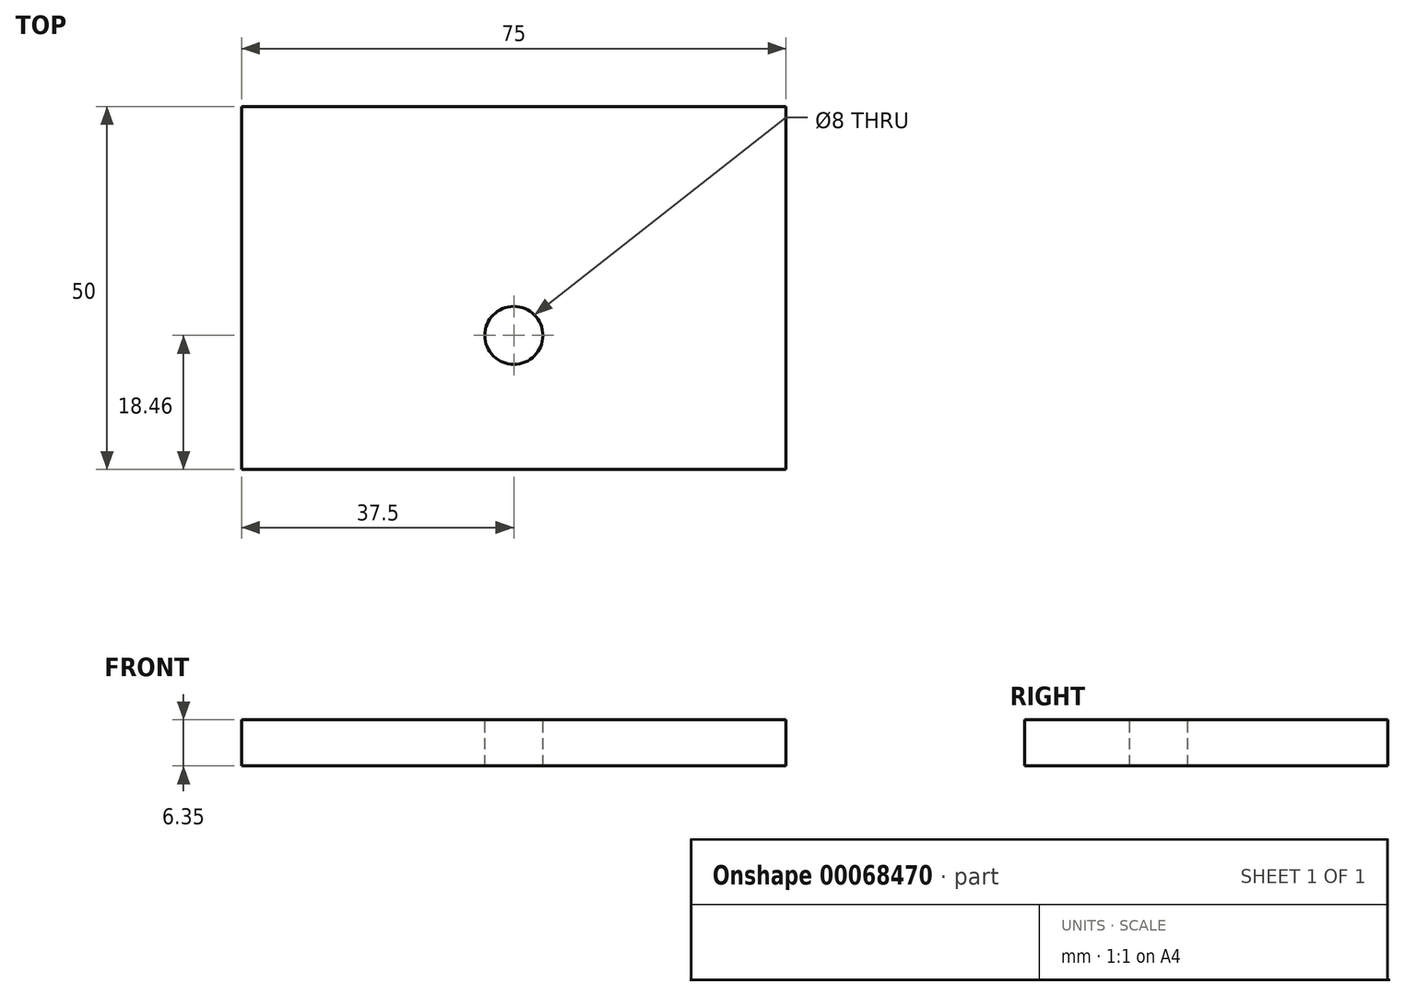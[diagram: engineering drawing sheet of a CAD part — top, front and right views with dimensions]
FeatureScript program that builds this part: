
annotation { "Feature Type Name" : "Feature", "Feature Type Description" : "" }
export const myFeature = defineFeature(function(context is Context, id is Id, definition is map)
    precondition{}
    {
        {
            var Q0;
            Q0=qCreatedBy(makeId("Top.planeOp"),FACE);
            var sketch = newSketch(context, id + "F0", { "sketchPlane" : qUnion([Q0])});
            skLineSegment(sketch, "E0.rect.bottom", {"start": v(37.5, 25) * mm, "end": v(-37.5, 25) * mm});
            skLineSegment(sketch, "E0.rect.top", {"start": v(37.5, -25) * mm, "end": v(-37.5, -25) * mm});
            skLineSegment(sketch, "E0.rect.left", {"start": v(37.5, 25) * mm, "end": v(37.5, -25) * mm});
            skLineSegment(sketch, "E0.rect.right", {"start": v(-37.5, 25) * mm, "end": v(-37.5, -25) * mm});
            skPoint(sketch, "E0.rect.middle", {"position": v(0, 0) * mm});
            skSolve(sketch);
        }
        {
            var Q0;
            Q0=makeQuery(id+"F0.imprint","IMPRINT",FACE,{"disambiguationData":[TD([[makeQuery(id+"F0.imprint","IMPRINT",EDGE,{"derivedFrom":sQuery(id+"F0.wireOp",EDGE,"E0.rect.bottom")}),1.0]])]});
            extrude(context, id + "F1", {"entities" : qUnion([Q0]), "depth" : 6.35 * mm});
        }
        {
            var Q0;
            Q0=makeQuery(id+"F1.opExtrude","CAP_FACE",FACE,{"disambiguationData":[OSD([sQuery(id+"F0.wireOp",EDGE,"E0.rect.bottom"),sQuery(id+"F0.wireOp",EDGE,"E0.rect.top"),sQuery(id+"F0.wireOp",EDGE,"E0.rect.left"),sQuery(id+"F0.wireOp",EDGE,"E0.rect.right")])],"isStart":false});
            var sketch = newSketch(context, id + "F2", { "sketchPlane" : qUnion([Q0])});
            skCircle(sketch, "E1", {"center": v(0, -6.54) * mm, "radius": 4 * mm});
            skPoint(sketch, "E2.end.orphan", {"position": v(0, -25) * mm});
            skPoint(sketch, "E2.start.orphan", {"position": v(0, -10.54) * mm});
            skLineSegment(sketch, "E3", {"start": v(0, -2.54) * mm, "end": v(0, 0) * mm});
            skLineSegment(sketch, "E4", {"start": v(0, -10.54) * mm, "end": v(0, -25) * mm});
            skSolve(sketch);
        }
        {
            var Q0;
            Q0=makeQuery(id+"F2.imprint","IMPRINT",FACE,{"disambiguationData":[TD([[makeQuery(id+"F2.imprint","IMPRINT",EDGE,{"derivedFrom":sQuery(id+"F2.wireOp",EDGE,"E1")}),1.0]])]});
            extrude(context, id + "F3", {"entities" : qUnion([Q0]), "operationType" : NewBodyOperationType.REMOVE, "endBound" : BoundingType.THROUGH_ALL, "oppositeDirection" : true, "depth" : 25 * mm});
        }
    });
